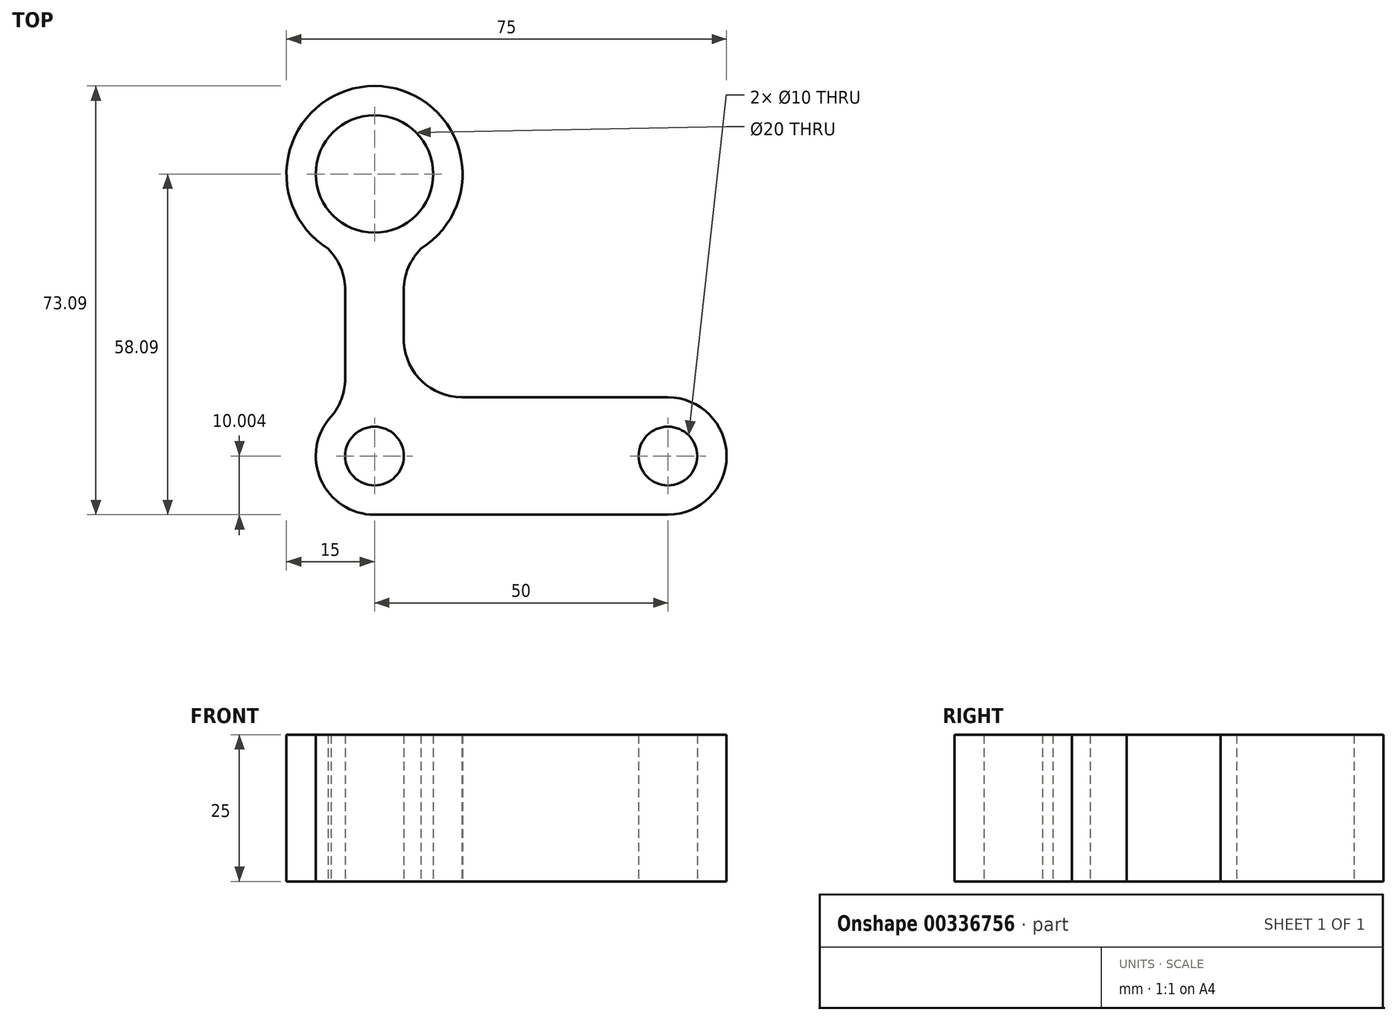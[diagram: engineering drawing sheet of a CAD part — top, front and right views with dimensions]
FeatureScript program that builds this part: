
annotation { "Feature Type Name" : "Feature", "Feature Type Description" : "" }
export const myFeature = defineFeature(function(context is Context, id is Id, definition is map)
    precondition{}
    {
        {
            var Q0;
            Q0=qCreatedBy(makeId("Top.planeOp"),FACE);
            var sketch = newSketch(context, id + "F0", { "sketchPlane" : qUnion([Q0])});
            skCircle(sketch, "E0", {"center": v(0, 0) * mm, "radius": 10 * mm});
            skCircle(sketch, "E1", {"center": v(0, 0) * mm, "radius": 15 * mm});
            skLineSegment(sketch, "E2", {"start": v(0, -10) * mm, "end": v(0, -15) * mm});
            skLineSegment(sketch, "E3", {"start": v(-5, -19.8) * mm, "end": v(-5, -14.14) * mm});
            skLineSegment(sketch, "E4", {"start": v(5, -19.8) * mm, "end": v(5, -14.14) * mm});
            skLineSegment(sketch, "E5", {"start": v(5, -14.14) * mm, "end": v(5, -19.8) * mm});
            skLineSegment(sketch, "E6", {"start": v(5, -19.8) * mm, "end": v(5, -28.74) * mm});
            skLineSegment(sketch, "E7", {"start": v(-5, -19.8) * mm, "end": v(-5, -39.43) * mm});
            skArc(sketch, "E8", {"start": v(-5, -19.8) * mm, "mid": v(-6.38, -14.74) * mm, "end": v(-10.13, -11.07) * mm});
            skArc(sketch, "E9", {"start": v(10.13, -11.07) * mm, "mid": v(6.38, -14.74) * mm, "end": v(5, -19.8) * mm});
            skArc(sketch, "E10", {"start": v(5, -39.43) * mm, "mid": v(-10, -48.09) * mm, "end": v(5, -56.75) * mm});
            skArc(sketch, "E11", {"start": v(50, -58.09) * mm, "mid": v(60, -48.09) * mm, "end": v(50, -38.09) * mm});
            skLineSegment(sketch, "E12", {"start": v(50, -48.09) * mm, "end": v(50, -38.09) * mm});
            skLineSegment(sketch, "E13", {"start": v(50, -38.09) * mm, "end": v(0, -38.09) * mm});
            skLineSegment(sketch, "E14", {"start": v(50, -48.09) * mm, "end": v(50, -58.09) * mm});
            skLineSegment(sketch, "E15", {"start": v(50, -58.09) * mm, "end": v(0, -58.09) * mm});
            skArc(sketch, "E16", {"start": v(5, -27.43) * mm, "mid": v(7.72, -34.96) * mm, "end": v(15.1, -38.09) * mm});
            skArc(sketch, "E17", {"start": v(-7.38, -41.34) * mm, "mid": v(-5.63, -38.36) * mm, "end": v(-5, -34.96) * mm});
            skLineSegment(sketch, "E18.trimOffspring", {"start": v(0, -58.09) * mm, "end": v(0, -67.49) * mm});
            skLineSegment(sketch, "E19.trimOffspring", {"start": v(5, -56.75) * mm, "end": v(5, -58.09) * mm});
            skLineSegment(sketch, "E20.trimOffspring", {"start": v(5, -38.09) * mm, "end": v(5, -39.43) * mm});
            skCircle(sketch, "E21", {"center": v(50, -48.09) * mm, "radius": 5 * mm});
            skCircle(sketch, "E22", {"center": v(0, -48.09) * mm, "radius": 5 * mm});
            skPoint(sketch, "E23.trimOffspring.end.orphan", {"position": v(-5, -59.05) * mm});
            skPoint(sketch, "E24.orphan", {"position": v(5, -59.05) * mm});
            skSolve(sketch);
        }
        {
            var Q0;
            Q0 = qSketchRegion(id + "F0", true);
            var Q1;
            {var subQ0=sQuery(id+"F0.wireOp",EDGE,"E20.trimOffspring");Q1=makeQuery(id+"F0.imprint","IMPRINT",FACE,{"disambiguationData":[TD([[makeQuery(id+"F0.imprint","IMPRINT",EDGE,{"derivedFrom":subQ0}),-1.0]])]});}
            extrude(context, id + "F1", {"entities" : qUnion([Q0, Q1]), "depth" : 25 * mm});
        }
    });
